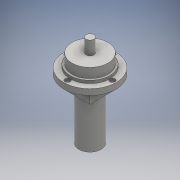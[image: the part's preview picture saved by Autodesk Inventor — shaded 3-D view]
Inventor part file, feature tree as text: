
AUTODESK INVENTOR PART (.ipt)
format: ipt  version: 2016 (Build 200138000, 138)  size: 167,936 bytes
history: native  units: mm
features: extrude x8, sketch x8, other x1
ambient origin geometry x8: Origin, YZ Plane, XZ Plane, XY Plane, X Axis, Y Axis, Z Axis, Center Point
bodies: Body1 (feature_tree)
feature tree (17):
  other  "ソリッド1"
  extrude  "押し出し1"  Depth=34.0mm
  extrude  "押し出し2"  Depth=73.0mm TaperAngle=0.0deg
  extrude  "押し出し3"  Depth=43.0mm
  extrude  "押し出し4"  Depth=43.0mm
  extrude  "押し出し5"  Depth=18.5mm TaperAngle=0.0deg
  extrude  "押し出し6"  Depth=80.0mm
  extrude  "押し出し7"  Depth=9.0mm TaperAngle=0.0deg
  extrude  "押し出し8"  Depth=61.0mm
  sketch  "スケッチ1"
  sketch  "スケッチ2"
  sketch  "スケッチ3"
  sketch  "スケッチ4"
  sketch  "スケッチ5"
  sketch  "スケッチ6"
  sketch  "スケッチ7"
  sketch  "スケッチ8"
